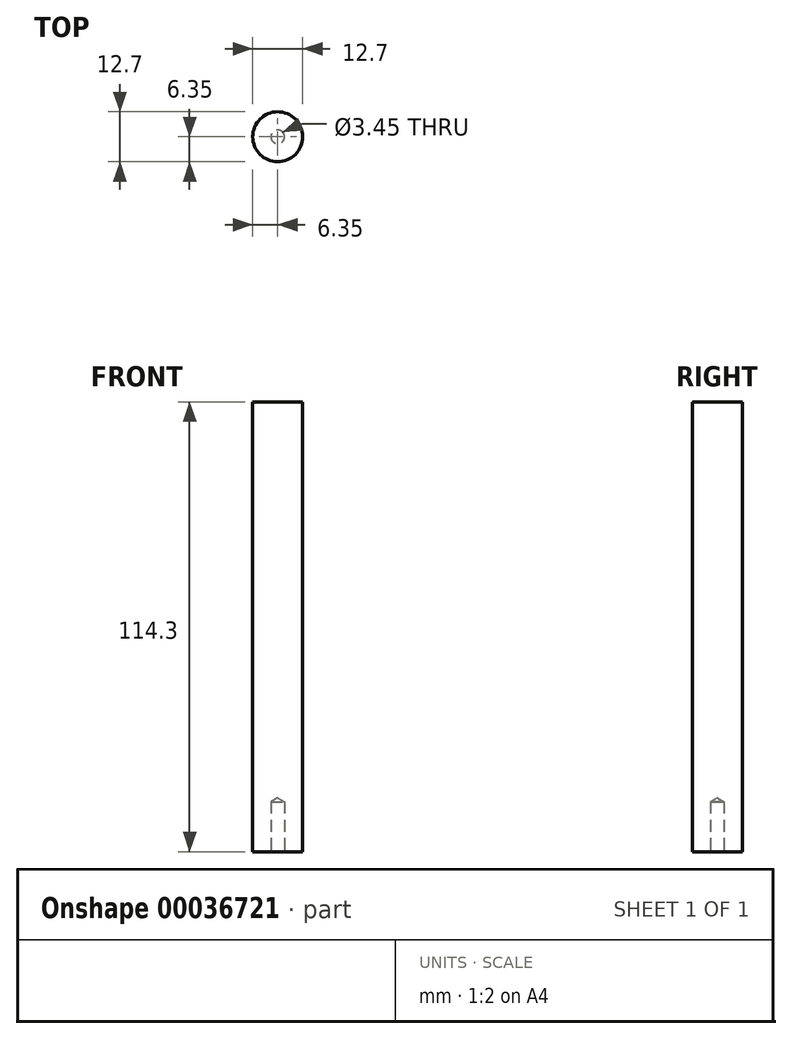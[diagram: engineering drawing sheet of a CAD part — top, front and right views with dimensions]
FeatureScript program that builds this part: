
annotation { "Feature Type Name" : "Feature", "Feature Type Description" : "" }
export const myFeature = defineFeature(function(context is Context, id is Id, definition is map)
    precondition{}
    {
        {
            var Q0;
            Q0=qCreatedBy(makeId("Top.planeOp"),FACE);
            var sketch = newSketch(context, id + "F0", { "sketchPlane" : qUnion([Q0])});
            skCircle(sketch, "E0", {"center": v(0, 0) * mm, "radius": 6.35 * mm});
            skSolve(sketch);
        }
        {
            var Q0;
            Q0 = qSketchRegion(id + "F0", true);
            extrude(context, id + "F1", {"entities" : qUnion([Q0]), "depth" : 114.3 * mm, "offsetDistance" : 25.4 * mm});
        }
        {
            var Q0;
            Q0=makeQuery(id+"F1.opExtrude","CAP_FACE",FACE,{"disambiguationData":[OSD([sQuery(id+"F0.wireOp",EDGE,"E0")])],"isStart":true});
            var sketch = newSketch(context, id + "F2", { "sketchPlane" : qUnion([Q0])});
            skPoint(sketch, "E1", {"position": v(0, 0) * mm});
            skSolve(sketch);
        }
        {
            var Q0;
            Q0=sQuery(id+"F2.wireOp",VERTEX,"E1");
            var Q1;
            Q1=makeQuery(id+"F1.opExtrude","SWEPT_BODY",BODY,{"disambiguationData":[OSD([sQuery(id+"F0.wireOp",EDGE,"E0")])]});
            hole(context, id + "F3", {"style" : HoleStyle.SIMPLE, "endStyle" : HoleEndStyle.BLIND, "standardTappedOrClearance" : lookupTablePath({ "standard" : "ANSI", "engagement" : "75%", "pitch" : "32 tpi", "size" : "#8", "type" : "Tapped" }), "standardBlindInLast" : lookupTablePath({ "standard" : "ANSI", "engagement" : "75%", "pitch" : "32 tpi", "size" : "#8", "type" : "Tapped" }), "holeDiameter" : 3.45 * mm, "majorDiameter" : 4.17 * mm, "showTappedDepth" : true, "holeDepth" : 12.7 * mm, "isTappedThrough" : true, "tappedDepth" : 10.32 * mm, "tapClearance" : 3, "locations" : qUnion([Q0]), "scope" : qUnion([Q1])});
        }
    });
